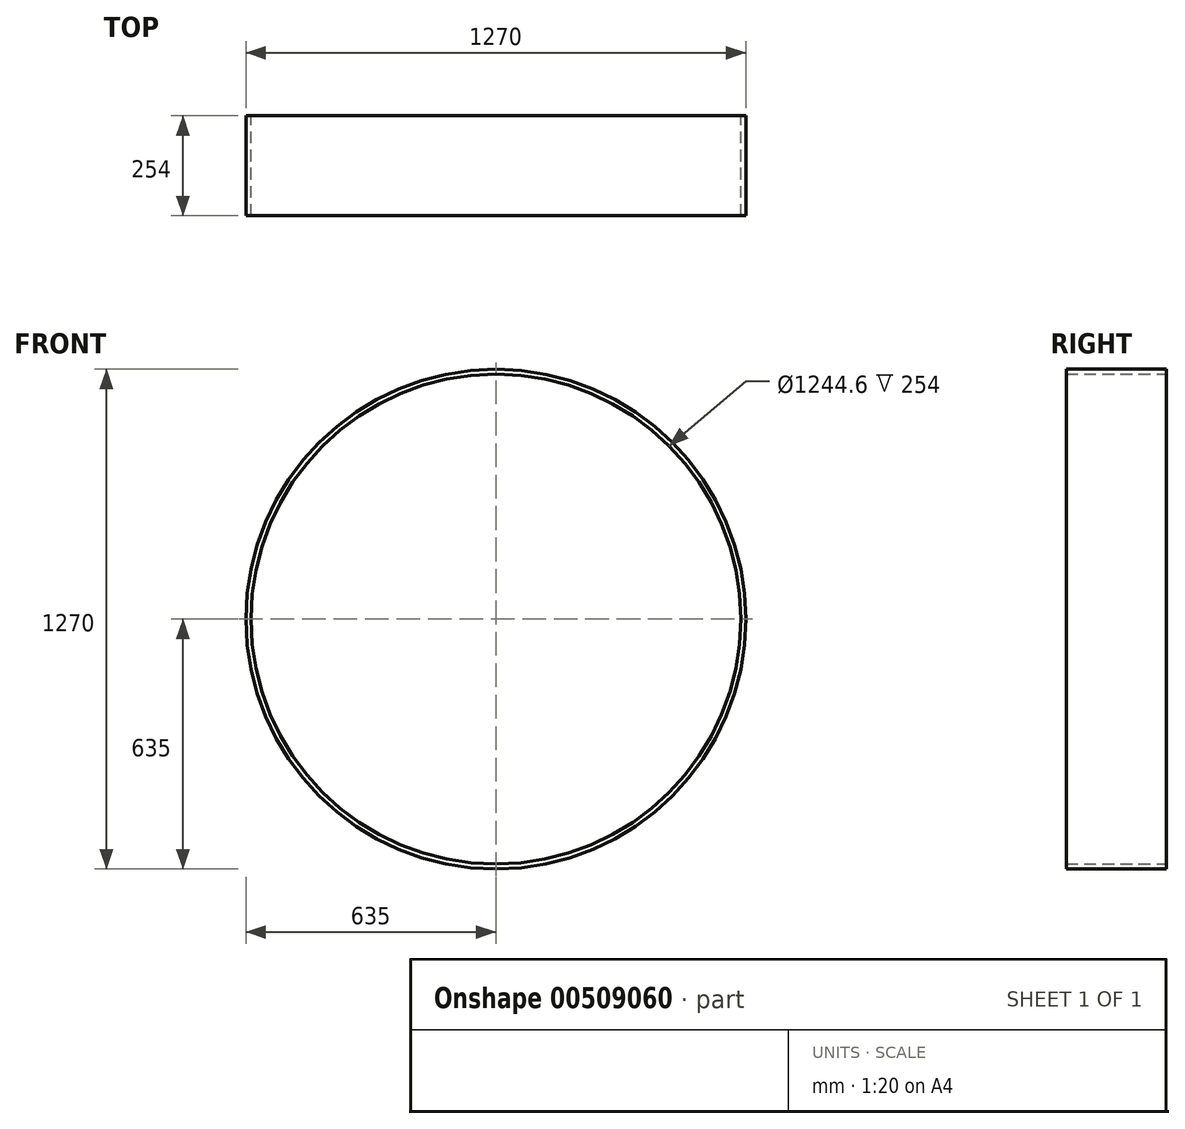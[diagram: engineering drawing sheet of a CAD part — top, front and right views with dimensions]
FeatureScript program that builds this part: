
annotation { "Feature Type Name" : "Feature", "Feature Type Description" : "" }
export const myFeature = defineFeature(function(context is Context, id is Id, definition is map)
    precondition{}
    {
        {
            var Q0;
            Q0=qCreatedBy(makeId("Front.planeOp"),FACE);
            var sketch = newSketch(context, id + "F0", { "sketchPlane" : qUnion([Q0])});
            skCircle(sketch, "E0", {"center": v(0, 0) * mm, "radius": 635 * mm});
            skCircle(sketch, "E1", {"center": v(0, 0) * mm, "radius": 622.3 * mm});
            skSolve(sketch);
        }
        {
            var Q0;
            Q0=makeQuery(id+"F0.imprint","IMPRINT",FACE,{"disambiguationData":[TD([[makeQuery(id+"F0.imprint","IMPRINT",EDGE,{"derivedFrom":sQuery(id+"F0.wireOp",EDGE,"E0")}),1.0]])]});
            extrude(context, id + "F1", {"entities" : qUnion([Q0]), "depth" : 254 * mm});
        }
    });
